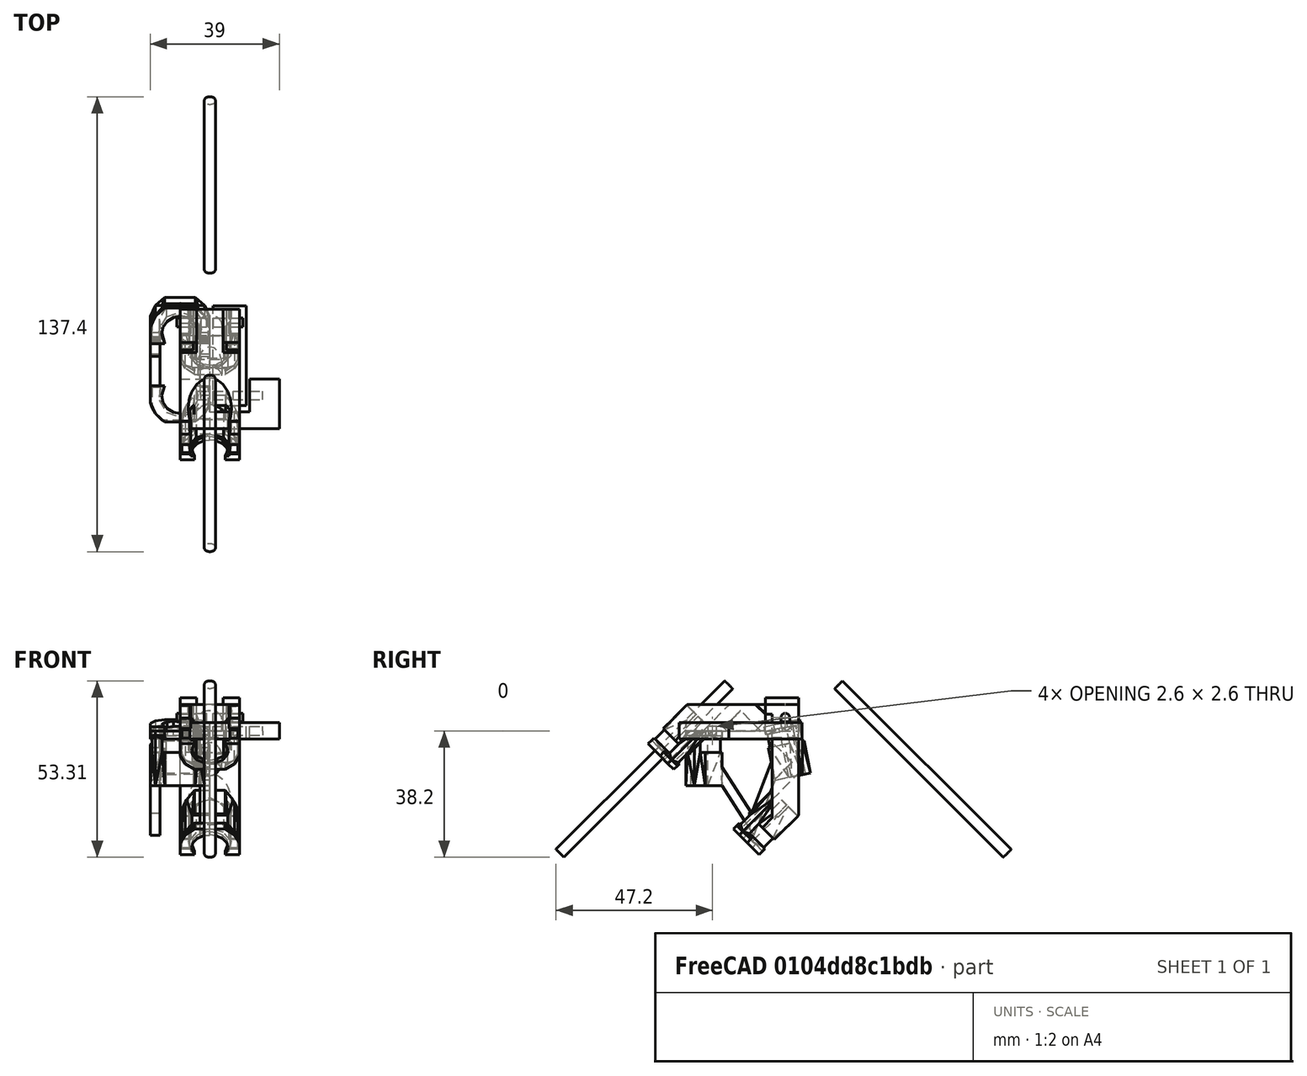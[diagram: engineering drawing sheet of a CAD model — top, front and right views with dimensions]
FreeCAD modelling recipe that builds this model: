
FCSTD DOCUMENT  (FreeCAD 0.18R16146 (Git))
Label: Solder Tweezer 2.0
License: All rights reserved
LicenseURL: http://en.wikipedia.org/wiki/All_rights_reserved
objects: Part::Box×20, Part::MultiFuse×16, Part::Cylinder×12, Part::Cut×11, Part::Feature×4, Part::Chamfer×4, Part::Fillet×2, Part::Fuse×2, Part::Sphere×2, Mesh::Feature×1, Part::Mirroring×1
note: 74 computed .brp shape members not serialized (recipe doc carries the construction recipe); baked Part::Feature solids carry a one-line shape summary decoded from their .brp

FEATURE [Mesh::Feature] print
FEATURE [Part::Feature] print001
  shape: bbox 18 x 37.62 x 34.94 mm, 432 faces, 0 solids (baked)
FEATURE [Part::Feature] print001_solid  label="print001 (Solid)"
  shape: bbox 18 x 37.62 x 34.94 mm, 432 faces (baked)
FEATURE [Part::Box] Box002  label="Cube002"
  AttacherType = Attacher::AttachEngine3D
  Height = 1.3
  Length = 9
  Placement = pos=(5,-1.3,0) rot=(0,0,1;0rad)
  Width = 2.6
FEATURE [Part::Box] Box  label="Cube"
  AttacherType = Attacher::AttachEngine3D
  Height = 5
  Length = 30
  Placement = pos=(0,-10,-2.5) rot=(0,0,1;0rad)
  Width = 15
FEATURE [Part::Box] Box001  label="Cube001"
  AttacherType = Attacher::AttachEngine3D
  Height = 5
  Length = 10
  Placement = pos=(10,-3,-2.5) rot=(0,0,1;0rad)
  Width = 30
FEATURE [Part::Box] Box004  label="Cube004"
  AttacherType = Attacher::AttachEngine3D
  Height = 1.3
  Length = 9
  Placement = pos=(5,-1.3,0) rot=(0,0,1;0rad)
  Width = 2.6
FEATURE [Part::Cylinder] Cylinder002
  Angle = 360
  AttacherType = Attacher::AttachEngine3D
  Height = 9
  Placement = pos=(5,0,0) rot=(0,1,0;1.5708rad)
  Radius = 1.3
FEATURE [Part::Box] Box003  label="Cube003"
  AttacherType = Attacher::AttachEngine3D
  Height = 5
  Length = 12
  Placement = pos=(9,-5,-2.5) rot=(0,0,1;0rad)
  Width = 30
FEATURE [Part::Cut] Cut
  Base = -> Box
  Tool = -> Box003
FEATURE [Part::MultiFuse] Fusion003
  Shapes = -> [Cut,Box001]
FEATURE [Part::Cylinder] Cylinder001
  Angle = 360
  AttacherType = Attacher::AttachEngine3D
  Height = 9
  Placement = pos=(5,0,0) rot=(0,1,0;1.5708rad)
  Radius = 1.3
FEATURE [Part::MultiFuse] Fusion
  Shapes = -> [Cylinder001,Box002]
FEATURE [Part::MultiFuse] Fusion001
  Placement = pos=(11,0,0) rot=(0,0,1;0rad)
  Shapes = -> [Cylinder002,Box004]
FEATURE [Part::MultiFuse] Fusion002
  Shapes = -> [Fusion,Fusion001]
FEATURE [Part::Cut] Cut001
  Base = -> Fusion003
  Tool = -> Fusion002
FEATURE [Part::Feature] print001_solid001  label="print001 (Solid)001"
  shape: bbox 18 x 37.62 x 34.94 mm, 432 faces (baked)
FEATURE [Part::Box] Box005  label="Cube005"
  AttacherType = Attacher::AttachEngine3D
  Height = 40
  Length = 31
  Placement = pos=(-14,3,-34) rot=(0,0,1;0rad)
  Width = 29
FEATURE [Part::Cut] Cut002
  Base = -> print001_solid001
  Placement = pos=(9,-17.3241,-6.01041) rot=(1,0,0;2.35619rad)
  Tool = -> Box005
FEATURE [Part::Box] Box006  label="Cube006"
  AttacherType = Attacher::AttachEngine3D
  Height = 8
  Length = 18
  Placement = pos=(0,-8,0) rot=(0,0,1;0rad)
  Width = 34
FEATURE [Part::Cylinder] Cylinder
  Angle = 360
  AttacherType = Attacher::AttachEngine3D
  Height = 9
  Placement = pos=(-1,22,4) rot=(0,1,0;1.5708rad)
  Radius = 1.3
FEATURE [Part::Cylinder] Cylinder003
  Angle = 360
  AttacherType = Attacher::AttachEngine3D
  Height = 59
  Placement = pos=(9,-21,-9) rot=(-1,0,0;0.785398rad)
  Radius = 6.5
FEATURE [Part::Cut] Cut003
  Base = -> Box006
  Tool = -> Cylinder003
FEATURE [Part::Fillet] Fillet
  Base = -> Cut003
  Edges = 2 edges r=0.75: [Edge7,Edge10]
FEATURE [Part::Box] Box007  label="Cube007"
  AttacherType = Attacher::AttachEngine3D
  Height = 1.3
  Length = 9
  Placement = pos=(-1,20.7,2.7) rot=(0,0,1;0rad)
  Width = 2.6
FEATURE [Part::Box] Box008  label="Cube008"
  AttacherType = Attacher::AttachEngine3D
  Height = 10
  Length = 5
  Placement = pos=(0,16,0) rot=(0,0,1;0rad)
  Width = 10
FEATURE [Part::Box] Box009  label="Cube009"
  AttacherType = Attacher::AttachEngine3D
  Height = 10
  Length = 5
  Placement = pos=(13,16,0) rot=(0,0,1;0rad)
  Width = 10
FEATURE [Part::MultiFuse] Fusion004
  Shapes = -> [Box008,Box009]
FEATURE [Part::Cut] Cut004
  Base = -> Fillet
  Tool = -> Fusion004
FEATURE [Part::MultiFuse] Fusion005  label="Square Topped Hole"
  Shapes = -> [Cylinder,Box007]
FEATURE [Part::Box] Box010  label="Cube010"
  AttacherType = Attacher::AttachEngine3D
  Height = 1.3
  Length = 9
  Placement = pos=(-1,20.7,2.7) rot=(0,0,1;0rad)
  Width = 2.6
FEATURE [Part::Cylinder] Cylinder004
  Angle = 360
  AttacherType = Attacher::AttachEngine3D
  Height = 9
  Placement = pos=(-1,22,4) rot=(0,1,0;1.5708rad)
  Radius = 1.3
FEATURE [Part::MultiFuse] Fusion006  label="Square Topped Hole001"
  Placement = pos=(11,0,0) rot=(0,0,1;0rad)
  Shapes = -> [Cylinder004,Box010]
FEATURE [Part::MultiFuse] Fusion007
  Shapes = -> [Fusion005,Fusion006]
FEATURE [Part::Cut] Cut005
  Base = -> Cut004
  Tool = -> Fusion007
FEATURE [Part::Fuse] Fusion008  label="Part 1"
  Base = -> Cut002
  Tool = -> Cut005
FEATURE [Part::Feature] print001_solid002  label="print001 (Solid)002"
  shape: bbox 18 x 37.62 x 34.94 mm, 432 faces (baked)
FEATURE [Part::Box] Box011  label="Cube011"
  AttacherType = Attacher::AttachEngine3D
  Height = 40
  Length = 31
  Placement = pos=(-14,3,-34) rot=(0,0,1;0rad)
  Width = 29
FEATURE [Part::Cut] Cut006
  Base = -> print001_solid002
  Placement = pos=(9,-17.3241,-6.01041) rot=(1,0,0;2.35619rad)
  Tool = -> Box011
FEATURE [Part::Box] Box012  label="Cube012"
  AttacherType = Attacher::AttachEngine3D
  Height = 8
  Length = 18
  Placement = pos=(0,-8,0) rot=(0,0,1;0rad)
  Width = 34
FEATURE [Part::Cylinder] Cylinder005
  Angle = 360
  AttacherType = Attacher::AttachEngine3D
  Height = 9
  Placement = pos=(-1,22,4) rot=(0,1,0;1.5708rad)
  Radius = 1.3
FEATURE [Part::Cylinder] Cylinder006
  Angle = 360
  AttacherType = Attacher::AttachEngine3D
  Height = 59
  Placement = pos=(9,-21,-9) rot=(-1,0,0;0.785398rad)
  Radius = 6.5
FEATURE [Part::Cut] Cut007
  Base = -> Box012
  Tool = -> Cylinder006
FEATURE [Part::Fillet] Fillet001
  Base = -> Cut007
  Edges = 2 edges r=0.75: [Edge7,Edge10]
FEATURE [Part::Box] Box013  label="Cube013"
  AttacherType = Attacher::AttachEngine3D
  Height = 1.3
  Length = 9
  Placement = pos=(-1,20.7,2.7) rot=(0,0,1;0rad)
  Width = 2.6
FEATURE [Part::Box] Box014  label="Cube014"
  AttacherType = Attacher::AttachEngine3D
  Height = 10
  Length = 5
  Placement = pos=(0,16,0) rot=(0,0,1;0rad)
  Width = 10
FEATURE [Part::Box] Box015  label="Cube015"
  AttacherType = Attacher::AttachEngine3D
  Height = 10
  Length = 5
  Placement = pos=(13,16,0) rot=(0,0,1;0rad)
  Width = 10
FEATURE [Part::MultiFuse] Fusion009
  Shapes = -> [Box014,Box015]
FEATURE [Part::MultiFuse] Fusion010  label="Square Topped Hole002"
  Shapes = -> [Cylinder005,Box013]
FEATURE [Part::Box] Box016  label="Cube016"
  AttacherType = Attacher::AttachEngine3D
  Height = 1.3
  Length = 9
  Placement = pos=(-1,20.7,2.7) rot=(0,0,1;0rad)
  Width = 2.6
FEATURE [Part::Cylinder] Cylinder007
  Angle = 360
  AttacherType = Attacher::AttachEngine3D
  Height = 9
  Placement = pos=(-1,22,4) rot=(0,1,0;1.5708rad)
  Radius = 1.3
FEATURE [Part::MultiFuse] Fusion011  label="Square Topped Hole003"
  Placement = pos=(11,0,0) rot=(0,0,1;0rad)
  Shapes = -> [Cylinder007,Box016]
FEATURE [Part::MultiFuse] Fusion012
  Shapes = -> [Fusion010,Fusion011]
FEATURE [Part::Box] Box017  label="Cube017"
  AttacherType = Attacher::AttachEngine3D
  Height = 10
  Length = 10
  Placement = pos=(4,16,-1) rot=(0,0,1;0rad)
  Width = 11
FEATURE [Part::Cut] Cut008
  Base = -> Fillet001
  Tool = -> Box017
FEATURE [Part::Sphere] Sphere
  Angle1 = -90
  Angle2 = 90
  Angle3 = 360
  AttacherType = Attacher::AttachEngine3D
  Placement = pos=(4,22,4) rot=(0,0,1;0rad)
  Radius = 1.3
FEATURE [Part::Sphere] Sphere001
  Angle1 = -90
  Angle2 = 90
  Angle3 = 360
  AttacherType = Attacher::AttachEngine3D
  Placement = pos=(14,22,4) rot=(0,0,1;0rad)
  Radius = 1.3
FEATURE [Part::MultiFuse] Fusion013
  Shapes = -> [Sphere,Sphere001]
FEATURE [Part::Fuse] Fusion014
  Base = -> Cut008
  Tool = -> Fusion013
FEATURE [Part::MultiFuse] Fusion015
  Placement = pos=(18,18,-18) rot=(0,-0.707107,-0.707107;3.14159rad)
  Shapes = -> [Cut006,Fusion014]
FEATURE [Part::Cylinder] Cylinder008
  Angle = 360
  AttacherType = Attacher::AttachEngine3D
  Height = 72
  Placement = pos=(9,-46,-37) rot=(1,0,0;-0.785398rad)
  Radius = 1.7
FEATURE [Part::Cylinder] Cylinder009
  Angle = 360
  AttacherType = Attacher::AttachEngine3D
  Height = 72
  Placement = pos=(9,-46,-37) rot=(-1,0,0;0.785398rad)
  Radius = 1.7
FEATURE [Part::Mirroring] Part__Mirroring  label="Cylinder009 (Mirror #1)"
  Base = (0,0,0)
  Normal = (0,1,0)
  Placement = pos=(0,43,0) rot=(0,0,1;0rad)
  Source = -> Cylinder009
FEATURE [Part::Chamfer] Chamfer001
  Base = -> Fusion008
  Edges = 2 edges r=3: [Edge41,Edge44]
FEATURE [Part::Chamfer] Chamfer
  Base = -> Chamfer001
  Edges = 2 edges r=3: [Edge12,Edge22]
FEATURE [Part::Box] Box018  label="Cube018"
  AttacherType = Attacher::AttachEngine3D
  Height = 3
  Length = 4
  Placement = pos=(14,13.75,5) rot=(0,0,1;0rad)
  Width = 4.5
FEATURE [Part::Chamfer] Chamfer002
  Base = -> Box018
  Edges = 1 edges r=2.5: [Edge9]
FEATURE [Part::Cylinder] Cylinder010
  Angle = 360
  AttacherType = Attacher::AttachEngine3D
  Height = 22
  Placement = pos=(9,21.5,-12) rot=(1,0,0;0.785398rad)
  Radius = 3.6
FEATURE [Part::Cylinder] Cylinder011
  Angle = 360
  AttacherType = Attacher::AttachEngine3D
  Height = 22
  Placement = pos=(9,21.5,-12) rot=(1,0,0;0.785398rad)
  Radius = 3.6
FEATURE [Part::Cut] Cut009  label="Part 1 2.0"
  Base = -> Chamfer
  Tool = -> Cylinder011
FEATURE [Part::Box] Box019  label="Cube019"
  AttacherType = Attacher::AttachEngine3D
  Height = 3
  Length = 4
  Placement = pos=(14,13.75,5) rot=(0,0,1;0rad)
  Width = 4.5
FEATURE [Part::Chamfer] Chamfer003
  Base = -> Box019
  Edges = 1 edges r=2.5: [Edge9]
  Placement = pos=(-14,0,0) rot=(0,0,1;0rad)
FEATURE [Part::MultiFuse] Fusion016
  Shapes = -> [Chamfer003,Chamfer002]
FEATURE [Part::MultiFuse] Fusion017
  Shapes = -> [Fusion016,Fusion015]
FEATURE [Part::Cut] Cut010  label="Part 2 2.0"
  Base = -> Fusion017
  Tool = -> Cylinder010
